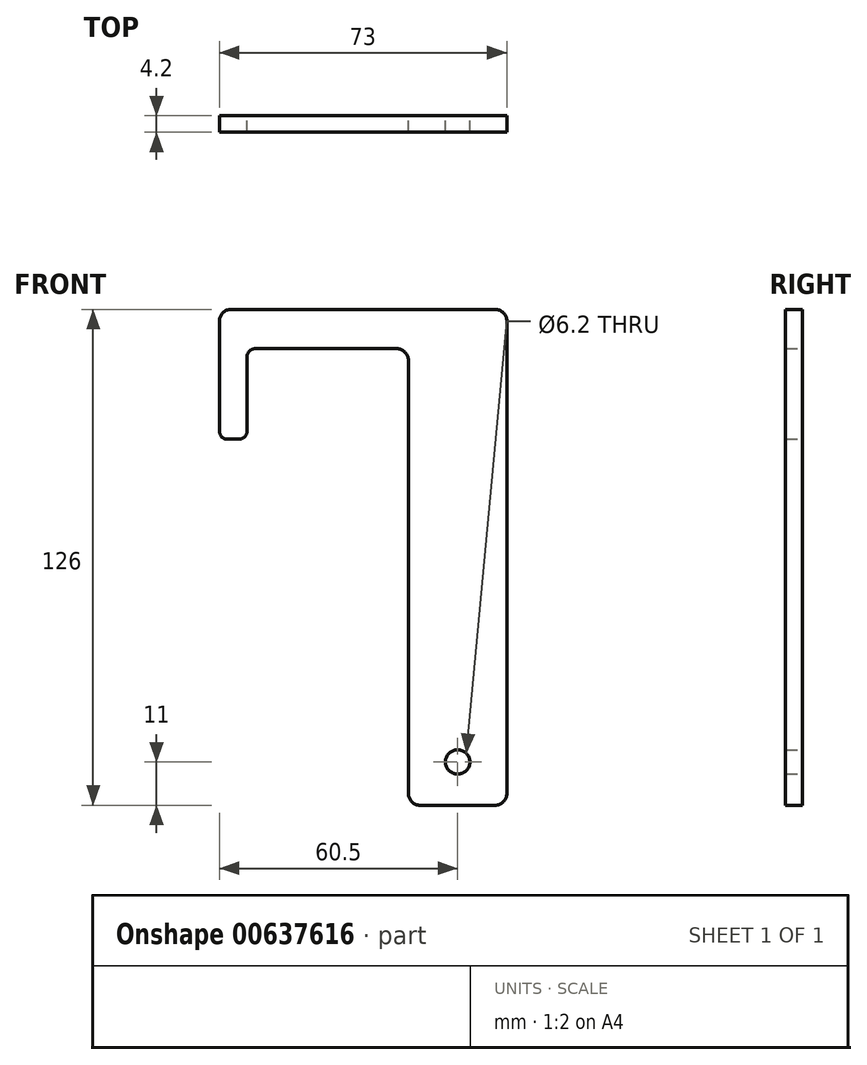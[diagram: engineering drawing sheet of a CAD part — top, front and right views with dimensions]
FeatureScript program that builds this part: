
annotation { "Feature Type Name" : "Feature", "Feature Type Description" : "" }
export const myFeature = defineFeature(function(context is Context, id is Id, definition is map)
    precondition{}
    {
        {
            var Q0;
            Q0=qCreatedBy(makeId("Front.planeOp"),FACE);
            var sketch = newSketch(context, id + "F0", { "sketchPlane" : qUnion([Q0])});
            skLineSegment(sketch, "E0", {"start": v(0, 2) * mm, "end": v(0, 21) * mm});
            skLineSegment(sketch, "E1", {"start": v(2, 23) * mm, "end": v(38, 23) * mm});
            skLineSegment(sketch, "E2", {"start": v(-2, 0) * mm, "end": v(-5, 0) * mm});
            skLineSegment(sketch, "E3", {"start": v(-7, 2) * mm, "end": v(-7, 30) * mm});
            skLineSegment(sketch, "E4", {"start": v(-4, 33) * mm, "end": v(63, 33) * mm});
            skCircle(sketch, "E5", {"center": v(53.5, -82) * mm, "radius": 3.1 * mm});
            skLineSegment(sketch, "E6", {"start": v(41, 20) * mm, "end": v(41, -90) * mm});
            skLineSegment(sketch, "E7", {"start": v(44, -93) * mm, "end": v(63, -93) * mm});
            skLineSegment(sketch, "E8", {"start": v(66, -90) * mm, "end": v(66, 30) * mm});
            skPoint(sketch, "E9.visualSharp", {"position": v(-7, 33) * mm});
            skArc(sketch, "E9.filletArc", {"start": v(-4, 33) * mm, "mid": v(-6.12, 32.12) * mm, "end": v(-7, 30) * mm});
            skPoint(sketch, "E10.visualSharp", {"position": v(0, 23) * mm});
            skArc(sketch, "E10.filletArc", {"start": v(2, 23) * mm, "mid": v(0.59, 22.41) * mm, "end": v(0, 21) * mm});
            skPoint(sketch, "E11.visualSharp", {"position": v(41, 23) * mm});
            skArc(sketch, "E11.filletArc", {"start": v(41, 20) * mm, "mid": v(40.12, 22.12) * mm, "end": v(38, 23) * mm});
            skPoint(sketch, "E12.visualSharp", {"position": v(66, 33) * mm});
            skArc(sketch, "E12.filletArc", {"start": v(66, 30) * mm, "mid": v(65.12, 32.12) * mm, "end": v(63, 33) * mm});
            skPoint(sketch, "E13.visualSharp", {"position": v(66, -93) * mm});
            skArc(sketch, "E13.filletArc", {"start": v(63, -93) * mm, "mid": v(65.12, -92.12) * mm, "end": v(66, -90) * mm});
            skPoint(sketch, "E14.visualSharp", {"position": v(41, -93) * mm});
            skArc(sketch, "E14.filletArc", {"start": v(41, -90) * mm, "mid": v(41.88, -92.12) * mm, "end": v(44, -93) * mm});
            skPoint(sketch, "E15.visualSharp", {"position": v(-7, 0) * mm});
            skArc(sketch, "E15.filletArc", {"start": v(-7, 2) * mm, "mid": v(-6.41, 0.59) * mm, "end": v(-5, 0) * mm});
            skPoint(sketch, "E16.visualSharp", {"position": v(0, 0) * mm});
            skArc(sketch, "E16.filletArc", {"start": v(-2, 0) * mm, "mid": v(-0.59, 0.59) * mm, "end": v(0, 2) * mm});
            skSolve(sketch);
        }
        {
            var Q0;
            Q0=makeQuery(id+"F0.imprint","IMPRINT",FACE,{"disambiguationData":[TD([[makeQuery(id+"F0.imprint","IMPRINT",EDGE,{"derivedFrom":sQuery(id+"F0.wireOp",EDGE,"E0")}),1.0]])]});
            extrude(context, id + "F1", {"entities" : qUnion([Q0]), "depth" : 4.2 * mm, "offsetDistance" : 25 * mm});
        }
    });
